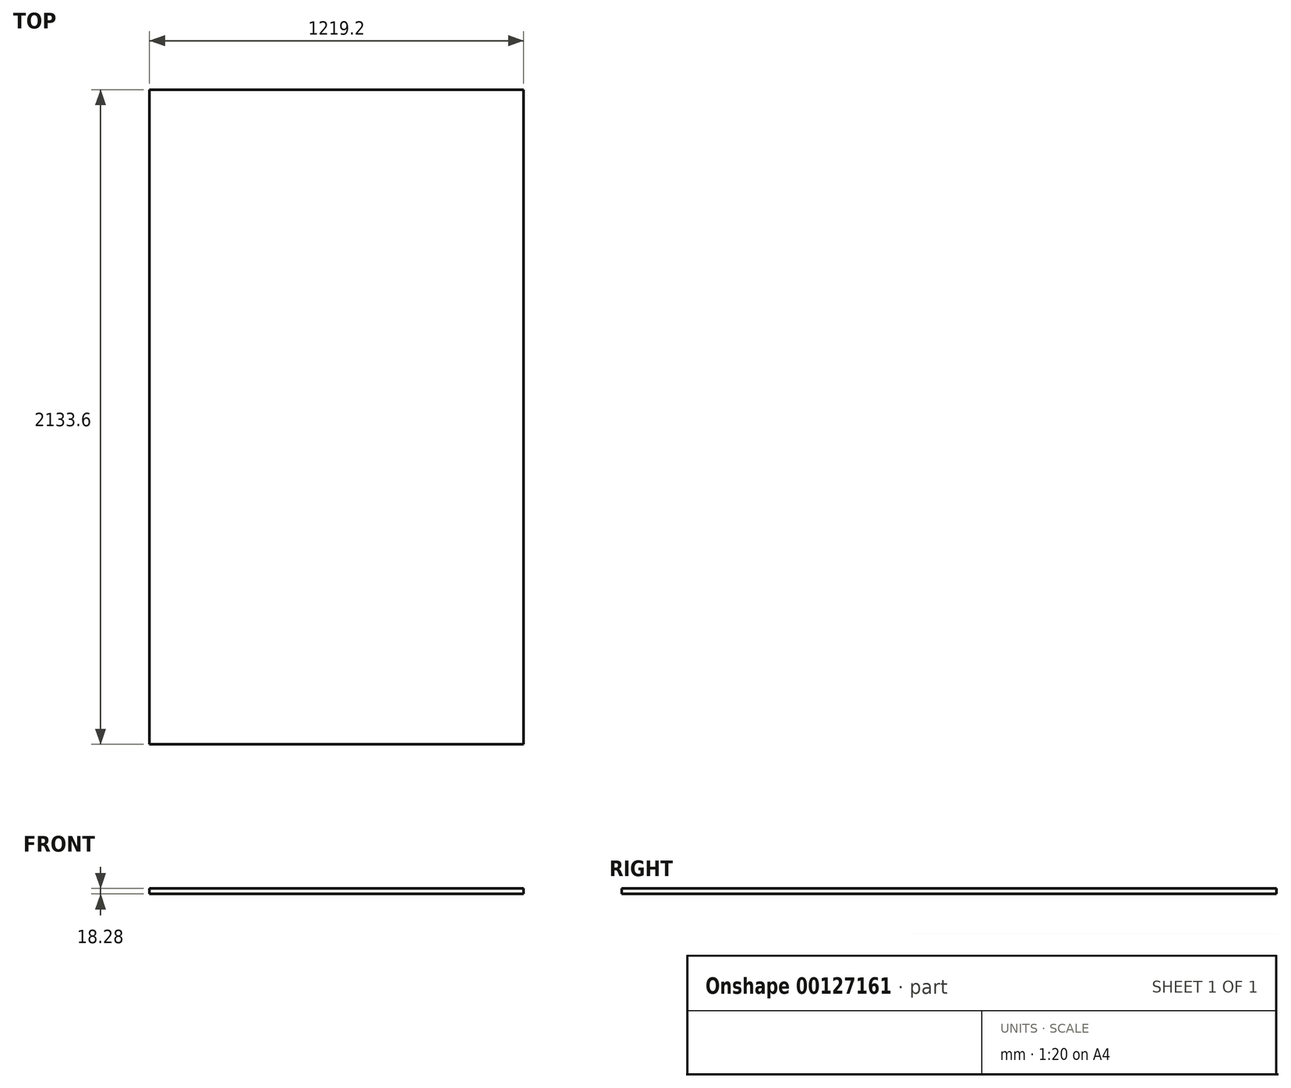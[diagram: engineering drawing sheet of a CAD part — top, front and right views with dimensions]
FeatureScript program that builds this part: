
annotation { "Feature Type Name" : "Feature", "Feature Type Description" : "" }
export const myFeature = defineFeature(function(context is Context, id is Id, definition is map)
    precondition{}
    {
        {
            var Q0;
            Q0=qCreatedBy(makeId("Front.planeOp"),FACE);
            var sketch = newSketch(context, id + "F0", { "sketchPlane" : qUnion([Q0])});
            skLineSegment(sketch, "E0.bottom", {"start": v(609.6, -9.14) * mm, "end": v(-609.6, -9.14) * mm});
            skLineSegment(sketch, "E0.top", {"start": v(609.6, 9.14) * mm, "end": v(-609.6, 9.14) * mm});
            skLineSegment(sketch, "E0.left", {"start": v(609.6, -9.14) * mm, "end": v(609.6, 9.14) * mm});
            skLineSegment(sketch, "E0.right", {"start": v(-609.6, -9.14) * mm, "end": v(-609.6, 9.14) * mm});
            skPoint(sketch, "E0.middle", {"position": v(0, 0) * mm});
            skSolve(sketch);
        }
        {
            var Q0;
            Q0=qSketchRegion(id+"F0",true);
            extrude(context, id + "F1", {"entities" : qUnion([Q0]), "depth" : 2133.6 * mm});
        }
    });
